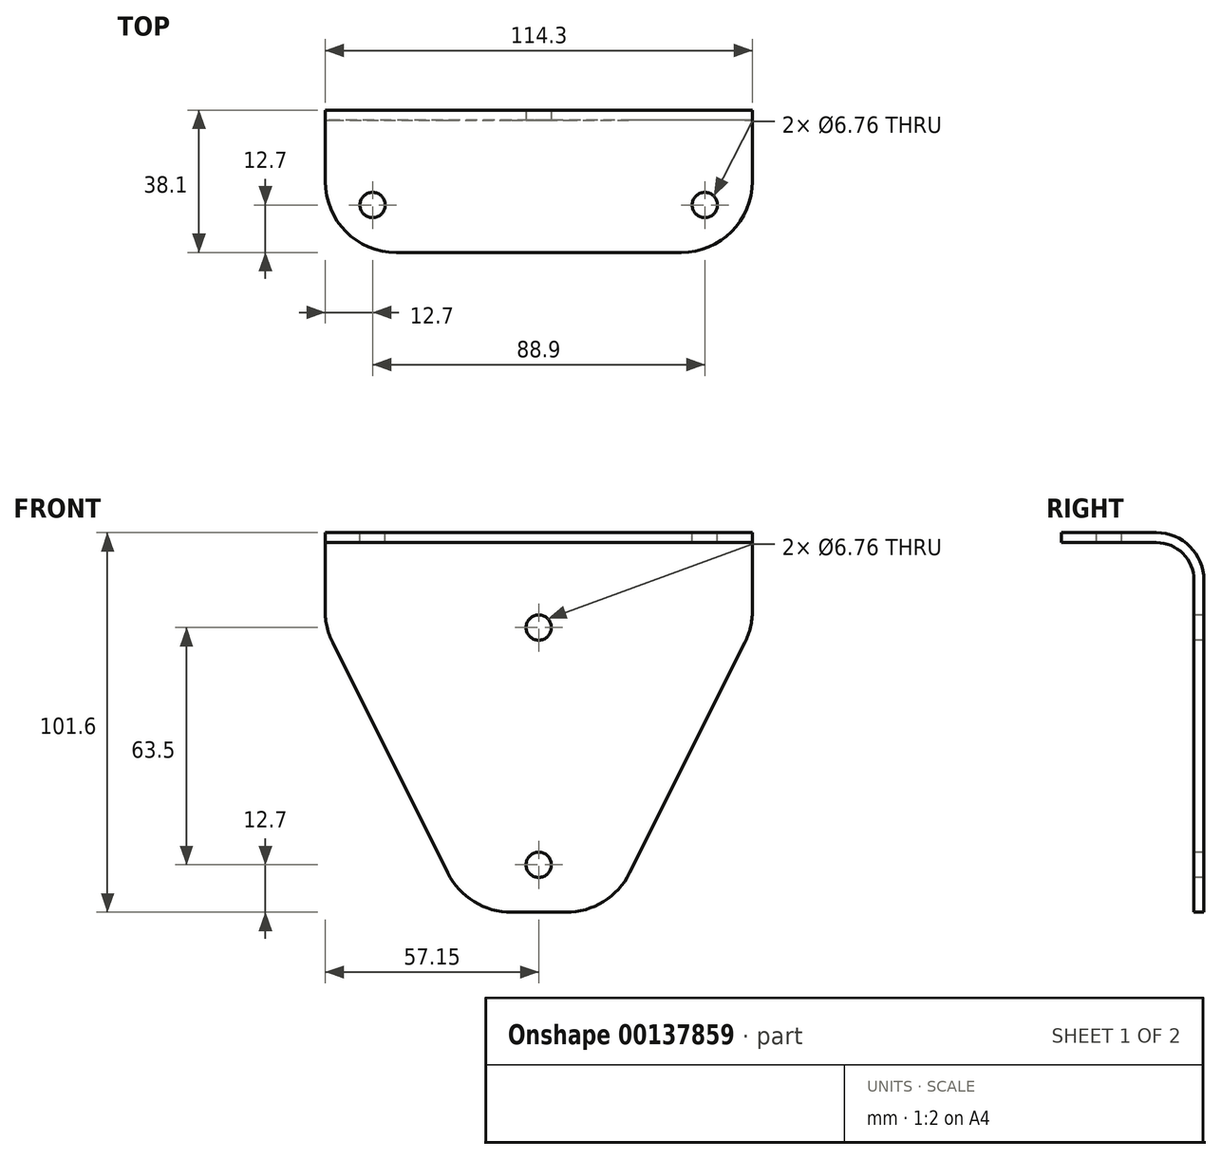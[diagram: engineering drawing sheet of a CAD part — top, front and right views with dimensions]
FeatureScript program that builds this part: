
annotation { "Feature Type Name" : "Feature", "Feature Type Description" : "" }
export const myFeature = defineFeature(function(context is Context, id is Id, definition is map)
    precondition{}
    {
        {
            var Q0;
            Q0=qCreatedBy(makeId("Top.planeOp"),FACE);
            var sketch = newSketch(context, id + "F0", { "sketchPlane" : qUnion([Q0])});
            skLineSegment(sketch, "E0.bottom", {"start": v(19.05, 19.05) * mm, "end": v(-19.05, 19.05) * mm, "construction": true});
            skLineSegment(sketch, "E0.top", {"start": v(19.05, -19.05) * mm, "end": v(-19.05, -19.05) * mm, "construction": true});
            skLineSegment(sketch, "E0.left", {"start": v(19.05, 19.05) * mm, "end": v(19.05, -19.05) * mm, "construction": true});
            skLineSegment(sketch, "E0.right", {"start": v(-19.05, 19.05) * mm, "end": v(-19.05, -19.05) * mm, "construction": true});
            skPoint(sketch, "E0.middle", {"position": v(0, 0) * mm});
            skSolve(sketch);
        }
        {
            var Q0;
            Q0=qCreatedBy(makeId("Front.planeOp"),FACE);
            cPlane(context, id + "F1", {"entities" : qUnion([Q0]), "cplaneType" : CPlaneType.OFFSET, "offset" : 19.05 * mm, "width" : 150 * mm, "height" : 150 * mm});
        }
        {
            var Q0;
            Q0=qCreatedBy(id+"F1.planeOp",FACE);
            var sketch = newSketch(context, id + "F2", { "sketchPlane" : qUnion([Q0])});
            skLineSegment(sketch, "E1", {"start": v(0, 0) * mm, "end": v(0, -45.36) * mm, "construction": true});
            skLineSegment(sketch, "E2", {"start": v(0, 0) * mm, "end": v(57.15, 0) * mm});
            skLineSegment(sketch, "E3", {"start": v(57.15, 0) * mm, "end": v(57.15, -25.4) * mm});
            skLineSegment(sketch, "E4", {"start": v(57.15, -25.4) * mm, "end": v(19.05, -101.6) * mm});
            skLineSegment(sketch, "E5", {"start": v(19.05, -101.6) * mm, "end": v(0, -101.6) * mm});
            skLineSegment(sketch, "E6.MirrorCS", {"start": v(0, 0) * mm, "end": v(-57.15, 0) * mm});
            skLineSegment(sketch, "E7.MirrorCS", {"start": v(-57.15, 0) * mm, "end": v(-57.15, -25.4) * mm});
            skLineSegment(sketch, "E8.MirrorCS", {"start": v(-57.15, -25.4) * mm, "end": v(-19.05, -101.6) * mm});
            skLineSegment(sketch, "E9.MirrorCS", {"start": v(-19.05, -101.6) * mm, "end": v(0, -101.6) * mm});
            skSolve(sketch);
        }
        {
            var Q0;
            Q0=qSketchRegion(id+"F2",true);
            extrude(context, id + "F3", {"entities" : qUnion([Q0]), "depth" : 2.65 * mm});
        }
        {
            var Q0;
            Q0=makeQuery(id+"F3.opExtrude","SWEPT_FACE",FACE,{"disambiguationData":[OSD([sQuery(id+"F2.wireOp",EDGE,"E2"),sQuery(id+"F2.wireOp",EDGE,"E6.MirrorCS")])]});
            var sketch = newSketch(context, id + "F4", { "sketchPlane" : qUnion([Q0])});
            skLineSegment(sketch, "E10.bottom", {"start": v(-57.15, -19.05) * mm, "end": v(57.15, -19.05) * mm});
            skLineSegment(sketch, "E10.top", {"start": v(-57.15, -57.15) * mm, "end": v(57.15, -57.15) * mm});
            skLineSegment(sketch, "E10.left", {"start": v(-57.15, -19.05) * mm, "end": v(-57.15, -57.15) * mm});
            skLineSegment(sketch, "E10.right", {"start": v(57.15, -19.05) * mm, "end": v(57.15, -57.15) * mm});
            skSolve(sketch);
        }
        {
            var Q0;
            Q0=qSketchRegion(id+"F4",true);
            extrude(context, id + "F5", {"entities" : qUnion([Q0]), "operationType" : NewBodyOperationType.ADD, "oppositeDirection" : true, "depth" : 2.65 * mm});
        }
        {
            var Q0;
            Q0=makeQuery(id+"F5.boolean.opBoolean","INTERSECT",EDGE,{"derivedFrom":[makeQuery(id+"F3.opExtrude","CAP_FACE",FACE,{"disambiguationData":[OSD([sQuery(id+"F2.wireOp",EDGE,"E2"),sQuery(id+"F2.wireOp",EDGE,"E3"),sQuery(id+"F2.wireOp",EDGE,"E4"),sQuery(id+"F2.wireOp",EDGE,"E5"),sQuery(id+"F2.wireOp",EDGE,"E6.MirrorCS"),sQuery(id+"F2.wireOp",EDGE,"E7.MirrorCS"),sQuery(id+"F2.wireOp",EDGE,"E8.MirrorCS"),sQuery(id+"F2.wireOp",EDGE,"E9.MirrorCS")])],"isStart":false}),makeQuery(id+"F5.opExtrude","CAP_FACE",FACE,{"disambiguationData":[OSD([sQuery(id+"F4.wireOp",EDGE,"E10.bottom"),sQuery(id+"F4.wireOp",EDGE,"E10.top"),sQuery(id+"F4.wireOp",EDGE,"E10.left"),sQuery(id+"F4.wireOp",EDGE,"E10.right")])],"isStart":false})]});
            fillet(context, id + "F6", {"entities" : qUnion([Q0]), "radius" : 10.05 * mm, "tangentPropagation" : true, "allowEdgeOverflow" : false});
        }
        {
            var Q0;
            Q0=makeQuery(id+"F3.opExtrude","CAP_EDGE",EDGE,{"disambiguationData":[OSD([sQuery(id+"F2.wireOp",EDGE,"E2"),sQuery(id+"F2.wireOp",EDGE,"E6.MirrorCS")])],"isStart":true});
            fillet(context, id + "F7", {"entities" : qUnion([Q0]), "radius" : 12.7 * mm, "tangentPropagation" : true, "allowEdgeOverflow" : false});
        }
        {
            var Q0;
            Q0=makeQuery(id+"F5.opExtrude","SWEPT_EDGE",EDGE,{"disambiguationData":[OSD([sQuery(id+"F4.wireOp",EDGE,"E10.top"),sQuery(id+"F4.wireOp",EDGE,"E10.left")])]});
            var Q1;
            Q1=makeQuery(id+"F5.opExtrude","SWEPT_EDGE",EDGE,{"disambiguationData":[OSD([sQuery(id+"F4.wireOp",EDGE,"E10.top"),sQuery(id+"F4.wireOp",EDGE,"E10.right")])]});
            var Q2;
            Q2=makeQuery(id+"F3.opExtrude","SWEPT_EDGE",EDGE,{"disambiguationData":[OSD([sQuery(id+"F2.wireOp",EDGE,"E7.MirrorCS"),sQuery(id+"F2.wireOp",EDGE,"E8.MirrorCS")])]});
            var Q3;
            Q3=makeQuery(id+"F3.opExtrude","SWEPT_EDGE",EDGE,{"disambiguationData":[OSD([sQuery(id+"F2.wireOp",EDGE,"E3"),sQuery(id+"F2.wireOp",EDGE,"E4")])]});
            var Q4;
            Q4=makeQuery(id+"F3.opExtrude","SWEPT_EDGE",EDGE,{"disambiguationData":[OSD([sQuery(id+"F2.wireOp",EDGE,"E4"),sQuery(id+"F2.wireOp",EDGE,"E5")])]});
            var Q5;
            Q5=makeQuery(id+"F3.opExtrude","SWEPT_EDGE",EDGE,{"disambiguationData":[OSD([sQuery(id+"F2.wireOp",EDGE,"E8.MirrorCS"),sQuery(id+"F2.wireOp",EDGE,"E9.MirrorCS")])]});
            fillet(context, id + "F8", {"entities" : qUnion([Q0, Q1, Q2, Q3, Q4, Q5]), "radius" : 19.05 * mm, "tangentPropagation" : true, "allowEdgeOverflow" : false});
        }
        {
            var Q0;
            Q0=makeQuery(id+"F5.boolean.opBoolean","MERGE",FACE,{"derivedFrom":[makeQuery(id+"F3.opExtrude","SWEPT_FACE",FACE,{"disambiguationData":[OSD([sQuery(id+"F2.wireOp",EDGE,"E2"),sQuery(id+"F2.wireOp",EDGE,"E6.MirrorCS")])]}),makeQuery(id+"F5.opExtrude","CAP_FACE",FACE,{"disambiguationData":[OSD([sQuery(id+"F4.wireOp",EDGE,"E10.bottom"),sQuery(id+"F4.wireOp",EDGE,"E10.top"),sQuery(id+"F4.wireOp",EDGE,"E10.left"),sQuery(id+"F4.wireOp",EDGE,"E10.right")])],"isStart":true})]});
            var sketch = newSketch(context, id + "F9", { "sketchPlane" : qUnion([Q0])});
            skLineSegment(sketch, "E11", {"start": v(0, 0) * mm, "end": v(0, -41.5) * mm, "construction": true});
            skPoint(sketch, "E12", {"position": v(44.45, -44.45) * mm});
            skPoint(sketch, "E13.MirrorP", {"position": v(-44.45, -44.45) * mm});
            skSolve(sketch);
        }
        {
            var Q0;
            Q0=sQuery(id+"F9.wireOp",VERTEX,"E13.MirrorP");
            var Q1;
            Q1=sQuery(id+"F9.wireOp",VERTEX,"E12");
            var Q2;
            Q2=makeQuery(id+"F3.opExtrude","SWEPT_BODY",BODY,{"disambiguationData":[OSD([sQuery(id+"F2.wireOp",EDGE,"E2"),sQuery(id+"F2.wireOp",EDGE,"E3"),sQuery(id+"F2.wireOp",EDGE,"E4"),sQuery(id+"F2.wireOp",EDGE,"E5"),sQuery(id+"F2.wireOp",EDGE,"E6.MirrorCS"),sQuery(id+"F2.wireOp",EDGE,"E7.MirrorCS"),sQuery(id+"F2.wireOp",EDGE,"E8.MirrorCS"),sQuery(id+"F2.wireOp",EDGE,"E9.MirrorCS")])]});
            hole(context, id + "F10", {"style" : HoleStyle.SIMPLE, "endStyle" : HoleEndStyle.THROUGH, "standardTappedOrClearance" : lookupTablePath({ "standard" : "ANSI", "fit" : "Normal (ASME)", "size" : "1/4", "type" : "Clearance" }), "standardBlindInLast" : lookupTablePath({ "fit" : "Free", "standard" : "ANSI", "size" : "1/4", "type" : "Clearance" }), "holeDiameter" : 6.76 * mm, "locations" : qUnion([Q0, Q1]), "scope" : qUnion([Q2]), "isTappedThrough" : true});
        }
        {
            var Q0;
            Q0=makeQuery(id+"F3.opExtrude","CAP_FACE",FACE,{"disambiguationData":[OSD([sQuery(id+"F2.wireOp",EDGE,"E2"),sQuery(id+"F2.wireOp",EDGE,"E3"),sQuery(id+"F2.wireOp",EDGE,"E4"),sQuery(id+"F2.wireOp",EDGE,"E5"),sQuery(id+"F2.wireOp",EDGE,"E6.MirrorCS"),sQuery(id+"F2.wireOp",EDGE,"E7.MirrorCS"),sQuery(id+"F2.wireOp",EDGE,"E8.MirrorCS"),sQuery(id+"F2.wireOp",EDGE,"E9.MirrorCS")])],"isStart":false});
            var sketch = newSketch(context, id + "F11", { "sketchPlane" : qUnion([Q0])});
            skLineSegment(sketch, "E14", {"start": v(0, -57.15) * mm, "end": v(22.02, -57.15) * mm, "construction": true});
            skPoint(sketch, "E15", {"position": v(0, -25.4) * mm});
            skPoint(sketch, "E16.MirrorP", {"position": v(0, -88.9) * mm});
            skSolve(sketch);
        }
        {
            var Q0;
            Q0=sQuery(id+"F11.wireOp",VERTEX,"E15");
            var Q1;
            Q1=sQuery(id+"F11.wireOp",VERTEX,"E16.MirrorP");
            var Q2;
            Q2=makeQuery(id+"F3.opExtrude","SWEPT_BODY",BODY,{"disambiguationData":[OSD([sQuery(id+"F2.wireOp",EDGE,"E2"),sQuery(id+"F2.wireOp",EDGE,"E3"),sQuery(id+"F2.wireOp",EDGE,"E4"),sQuery(id+"F2.wireOp",EDGE,"E5"),sQuery(id+"F2.wireOp",EDGE,"E6.MirrorCS"),sQuery(id+"F2.wireOp",EDGE,"E7.MirrorCS"),sQuery(id+"F2.wireOp",EDGE,"E8.MirrorCS"),sQuery(id+"F2.wireOp",EDGE,"E9.MirrorCS")])]});
            hole(context, id + "F12", {"style" : HoleStyle.SIMPLE, "endStyle" : HoleEndStyle.THROUGH, "standardTappedOrClearance" : lookupTablePath({ "standard" : "ANSI", "fit" : "Normal (ASME)", "size" : "1/4", "type" : "Clearance" }), "standardBlindInLast" : lookupTablePath({ "fit" : "Free", "standard" : "ANSI", "size" : "1/4", "type" : "Clearance" }), "holeDiameter" : 6.76 * mm, "locations" : qUnion([Q0, Q1]), "scope" : qUnion([Q2]), "isTappedThrough" : true});
        }
    });
